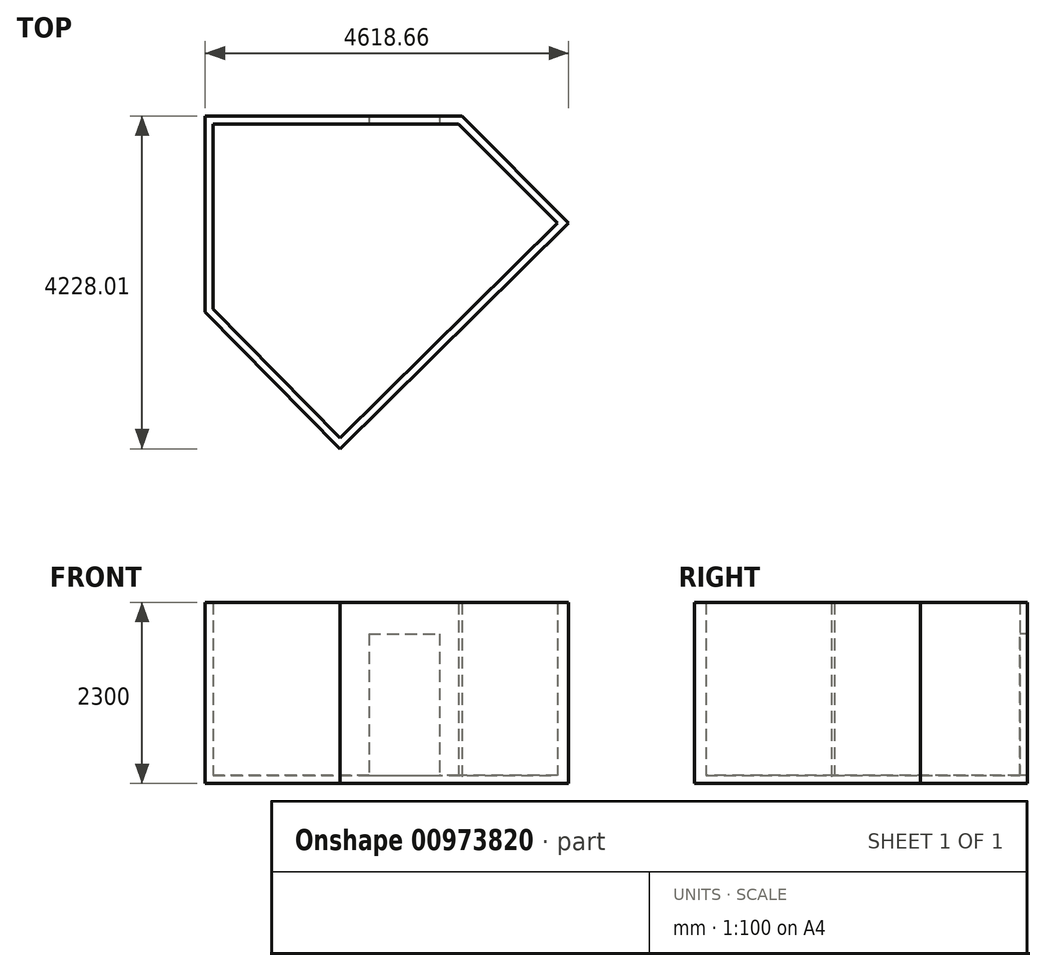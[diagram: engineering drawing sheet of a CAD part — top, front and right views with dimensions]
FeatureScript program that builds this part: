
annotation { "Feature Type Name" : "Feature", "Feature Type Description" : "" }
export const myFeature = defineFeature(function(context is Context, id is Id, definition is map)
    precondition{}
    {
        {
            var Q0;
            Q0=qCreatedBy(makeId("Top.planeOp"),FACE);
            var sketch = newSketch(context, id + "F0", { "sketchPlane" : qUnion([Q0])});
            skLineSegment(sketch, "E0", {"start": v(0, 0) * mm, "end": v(-2980, 0) * mm});
            skLineSegment(sketch, "E1", {"start": v(-2980, 0) * mm, "end": v(-2980, -2491.05) * mm});
            skLineSegment(sketch, "E2", {"start": v(-2980, -2491.05) * mm, "end": v(-1264.86, -4228) * mm});
            skLineSegment(sketch, "E3", {"start": v(-1264.86, -4228) * mm, "end": v(1638.66, -1360.95) * mm});
            skLineSegment(sketch, "E4", {"start": v(1638.66, -1360.95) * mm, "end": v(281.5, 0) * mm});
            skLineSegment(sketch, "E5", {"start": v(281.5, 0) * mm, "end": v(0, 0) * mm});
            skLineSegment(sketch, "E6.0", {"start": v(-2880, -100) * mm, "end": v(-2880, -2450) * mm});
            skLineSegment(sketch, "E6.1", {"start": v(-1263.96, -4086.59) * mm, "end": v(1496.9, -1360.4) * mm});
            skLineSegment(sketch, "E6.2", {"start": v(1496.9, -1360.4) * mm, "end": v(240, -100) * mm});
            skLineSegment(sketch, "E6.3", {"start": v(-2880, -2450) * mm, "end": v(-1263.96, -4086.59) * mm});
            skLineSegment(sketch, "E6.4", {"start": v(240, -100) * mm, "end": v(0, -100) * mm});
            skLineSegment(sketch, "E6.5", {"start": v(0, -100) * mm, "end": v(-2880, -100) * mm});
            skLineSegment(sketch, "E7", {"start": v(0, 0) * mm, "end": v(0, -100) * mm, "construction": true});
            skSolve(sketch);
        }
        {
            var Q0;
            Q0 = qSketchRegion(id + "F0", true);
            extrude(context, id + "F1", {"entities" : qUnion([Q0]), "depth" : 2200 * mm, "offsetDistance" : 25 * mm});
        }
        {
            var Q0;
            Q0=qCreatedBy(makeId("Top.planeOp"),FACE);
            var sketch = newSketch(context, id + "F2", { "sketchPlane" : qUnion([Q0])});
            skLineSegment(sketch, "E8.0", {"start": v(-1264.86, -4228) * mm, "end": v(1638.66, -1360.95) * mm});
            skLineSegment(sketch, "E8.1", {"start": v(-2980, -2491.05) * mm, "end": v(-1264.86, -4228) * mm});
            skLineSegment(sketch, "E8.2", {"start": v(-2980, 0) * mm, "end": v(-2980, -2491.05) * mm});
            skLineSegment(sketch, "E8.3", {"start": v(281.5, 0) * mm, "end": v(-2980, 0) * mm});
            skLineSegment(sketch, "E8.4", {"start": v(1638.66, -1360.95) * mm, "end": v(281.5, 0) * mm});
            skSolve(sketch);
        }
        {
            var Q0;
            Q0 = qSketchRegion(id + "F2", true);
            extrude(context, id + "F3", {"entities" : qUnion([Q0]), "operationType" : NewBodyOperationType.ADD, "oppositeDirection" : true, "depth" : 100 * mm, "offsetDistance" : 25 * mm});
        }
        {
            var Q0;
            Q0=makeQuery(id+"F1.opExtrude","SWEPT_FACE",FACE,{"disambiguationData":[OSD([sQuery(id+"F0.wireOp",EDGE,"E6.4"),sQuery(id+"F0.wireOp",EDGE,"E6.5")])]});
            var sketch = newSketch(context, id + "F4", { "sketchPlane" : qUnion([Q0])});
            skLineSegment(sketch, "E9.bottom", {"start": v(0, 0) * mm, "end": v(-900, 0) * mm});
            skLineSegment(sketch, "E9.top", {"start": v(0, 1800) * mm, "end": v(-900, 1800) * mm});
            skLineSegment(sketch, "E9.left", {"start": v(0, 0) * mm, "end": v(0, 1800) * mm});
            skLineSegment(sketch, "E9.right", {"start": v(-900, 0) * mm, "end": v(-900, 1800) * mm});
            skSolve(sketch);
        }
        {
            var Q0;
            Q0 = qSketchRegion(id + "F4", true);
            extrude(context, id + "F5", {"entities" : qUnion([Q0]), "operationType" : NewBodyOperationType.REMOVE, "endBound" : BoundingType.UP_TO_NEXT, "oppositeDirection" : true, "depth" : 25 * mm, "offsetDistance" : 25 * mm});
        }
    });
